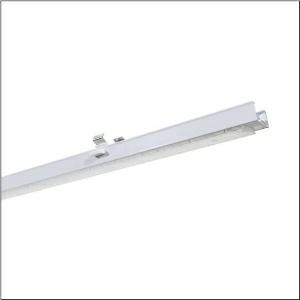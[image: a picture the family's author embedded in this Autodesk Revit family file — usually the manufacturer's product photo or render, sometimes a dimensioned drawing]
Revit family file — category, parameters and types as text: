
# Revit family: trunking_flex_31_51re12ma46b
name_source: partatom
category: Lighting Fixtures
units: mm (PartAtom-declared; Revit-internal decimal feet)

## family parameters
Cut with Voids When Loaded = No
Host = Face
Light Source = No
Part Type = Normal
Room Calculation Point = No
Round Connector Dimension = Use Diameter
Shared = No

## types (1)
- --- (1 x LED, 6400 lm, 40 W, 4000K)
    Apparent Load = 40 VA
    CIE Flux Codes = 65 91 98 99 100
    Color Rendering = 80
    Color Temperature = 4000K
    Default Elevation = 1800 mm
    Description = Trunking Flex 31, luminaire insert, of extruded aluminium section, coated, traffic white (RAL 9016), length: 1.172mm, width: 91mm, height: 53mm, LED rated luminous flux: 6.400lm, light colour: 840, control gear: ON/OFF Multilumen, with system connector: socket, mains connection: 220..240V, AC, 50/60Hz, rated input power: 40W, luminous flux adjustable on luminaire in four steps (3420/4540/5580/6630lm), connected load according to luminous flux setting (20/26/33/40W), primary light control with lens, of plastic, primary optical cover: cover, of PMMA, light emission: direct distribution, protection rating (complete): IP20, insulation class (complete): insulation class I (protective earthing), certification: CE, UKCA, impact resistance: IK02, permissible ambient temperature for indoor applications: -20..+40°C, packaging unit: 1 piece
    Height = 58 mm
    Lamp = 1 x LED
    Lamp Light Flux = 6400 lm
    Lamp Power = 40 W
    Lamp count = 1
    Length = 1172 mm
    Luminous efficacy = 160 lm/W
    Manufacturer = Siteco
    ModVariant = No
    Model = 51RE12MA46B
    Mounting Place = Ceiling
    Mounting Type = Pendant
    Number of Poles = 1
    OnlyDefault = Yes
    Power Factor = 1
    Product Name = Trunking Flex 31
    Product group = luminaire insert
    ProductGroupID = 902
    Protection Class = Protection class I
    Protection Degree = IP 20
    RLX_Detail_Level = 1
    RLX_Emergency_Light_Flux = 0 lm
    RLX_Emergency_Type = 0
    RLX_Emergency_Type_DB = No
    RlxData = <blob elided: 19945 chars, md5=8a662b30>
    Socket = socket
    Standby Power = 0 W
    System Light Flux = 6400 lm
    System Power = 40 W
    Type Comments = factory setting: luminous flux: 100 % | (ON | ON) | 300 mA
    Type Image = l_1266702.jpg
    URL = http://relux.com
    VarID = @adj_059190
    Voltage = 0 V
    Weight = 0.00 kg
    Width = 65 mm

## geometry (parser evidence)
native form markers: Blend x4, Sweep x12
no freeform markers — native parametric forms only
